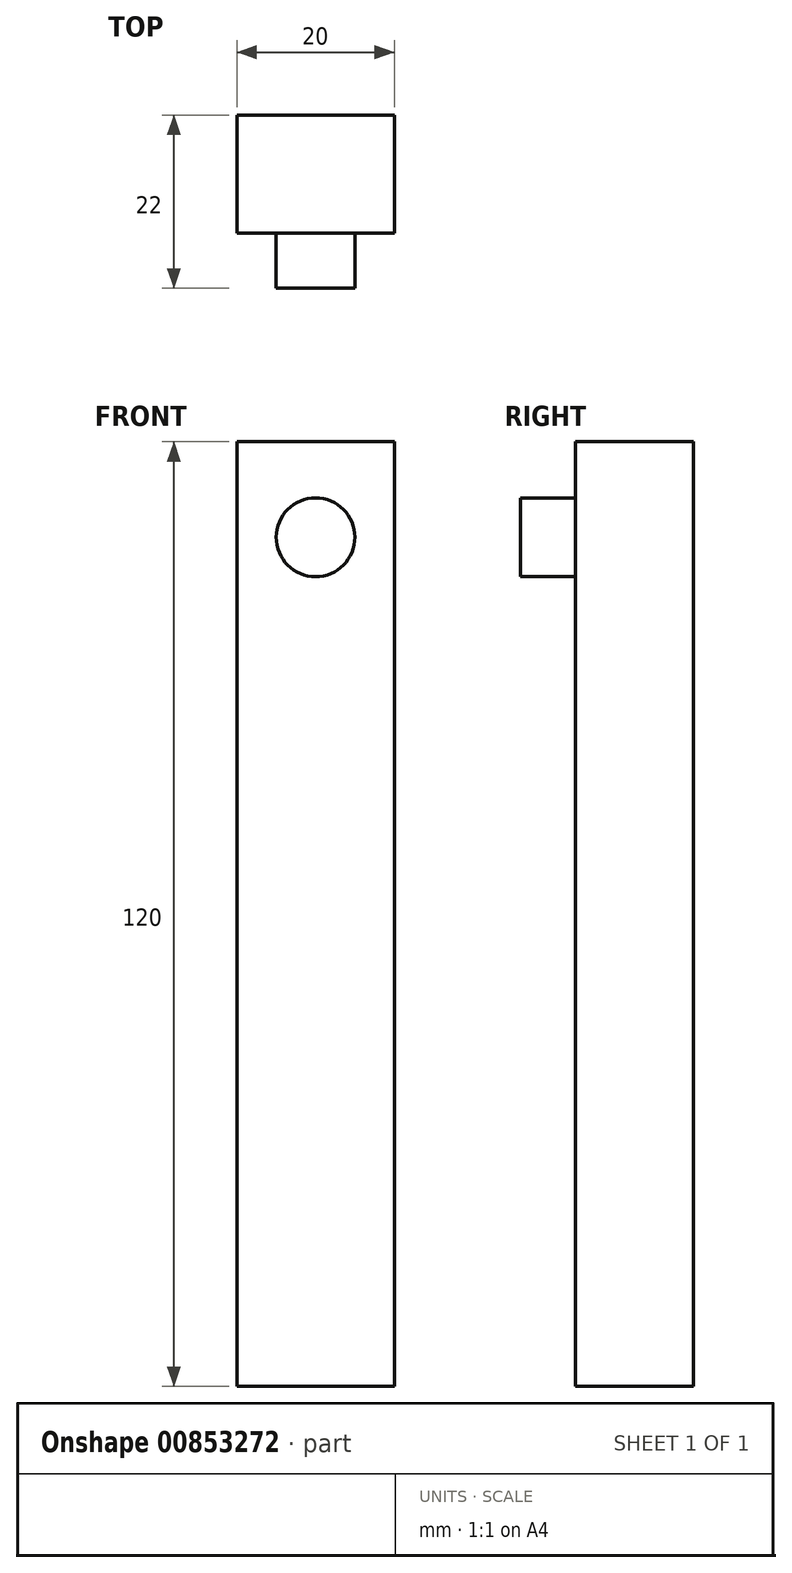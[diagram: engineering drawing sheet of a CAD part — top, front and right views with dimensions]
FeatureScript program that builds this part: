
annotation { "Feature Type Name" : "Feature", "Feature Type Description" : "" }
export const myFeature = defineFeature(function(context is Context, id is Id, definition is map)
    precondition{}
    {
        {
            var Q0;
            Q0=qCreatedBy(makeId("Top.planeOp"),FACE);
            var sketch = newSketch(context, id + "F0", { "sketchPlane" : qUnion([Q0])});
            skLineSegment(sketch, "E0.bottom", {"start": v(-10, 7.5) * mm, "end": v(10, 7.5) * mm});
            skLineSegment(sketch, "E0.top", {"start": v(-10, -7.5) * mm, "end": v(10, -7.5) * mm});
            skLineSegment(sketch, "E0.left", {"start": v(-10, 7.5) * mm, "end": v(-10, -7.5) * mm});
            skLineSegment(sketch, "E0.right", {"start": v(10, 7.5) * mm, "end": v(10, -7.5) * mm});
            skSolve(sketch);
        }
        {
            var Q0;
            Q0=makeQuery(id+"F0.imprint","IMPRINT",FACE,{"disambiguationData":[TD([[makeQuery(id+"F0.imprint","IMPRINT",EDGE,{"derivedFrom":sQuery(id+"F0.wireOp",EDGE,"E0.bottom")}),-1.0]])]});
            extrude(context, id + "F1", {"entities" : qUnion([Q0]), "depth" : 120 * mm, "offsetDistance" : 25 * mm});
        }
        {
            var Q0;
            Q0=makeQuery(id+"F1.opExtrude","SWEPT_FACE",FACE,{"disambiguationData":[OSD([sQuery(id+"F0.wireOp",EDGE,"E0.top")])]});
            var sketch = newSketch(context, id + "F2", { "sketchPlane" : qUnion([Q0])});
            skCircle(sketch, "E1", {"center": v(0, 107.87) * mm, "radius": 5 * mm});
            skSolve(sketch);
        }
        {
            var Q0;
            Q0 = qSketchRegion(id + "F2", true);
            extrude(context, id + "F3", {"entities" : qUnion([Q0]), "depth" : 7 * mm, "offsetDistance" : 25 * mm});
        }
    });
